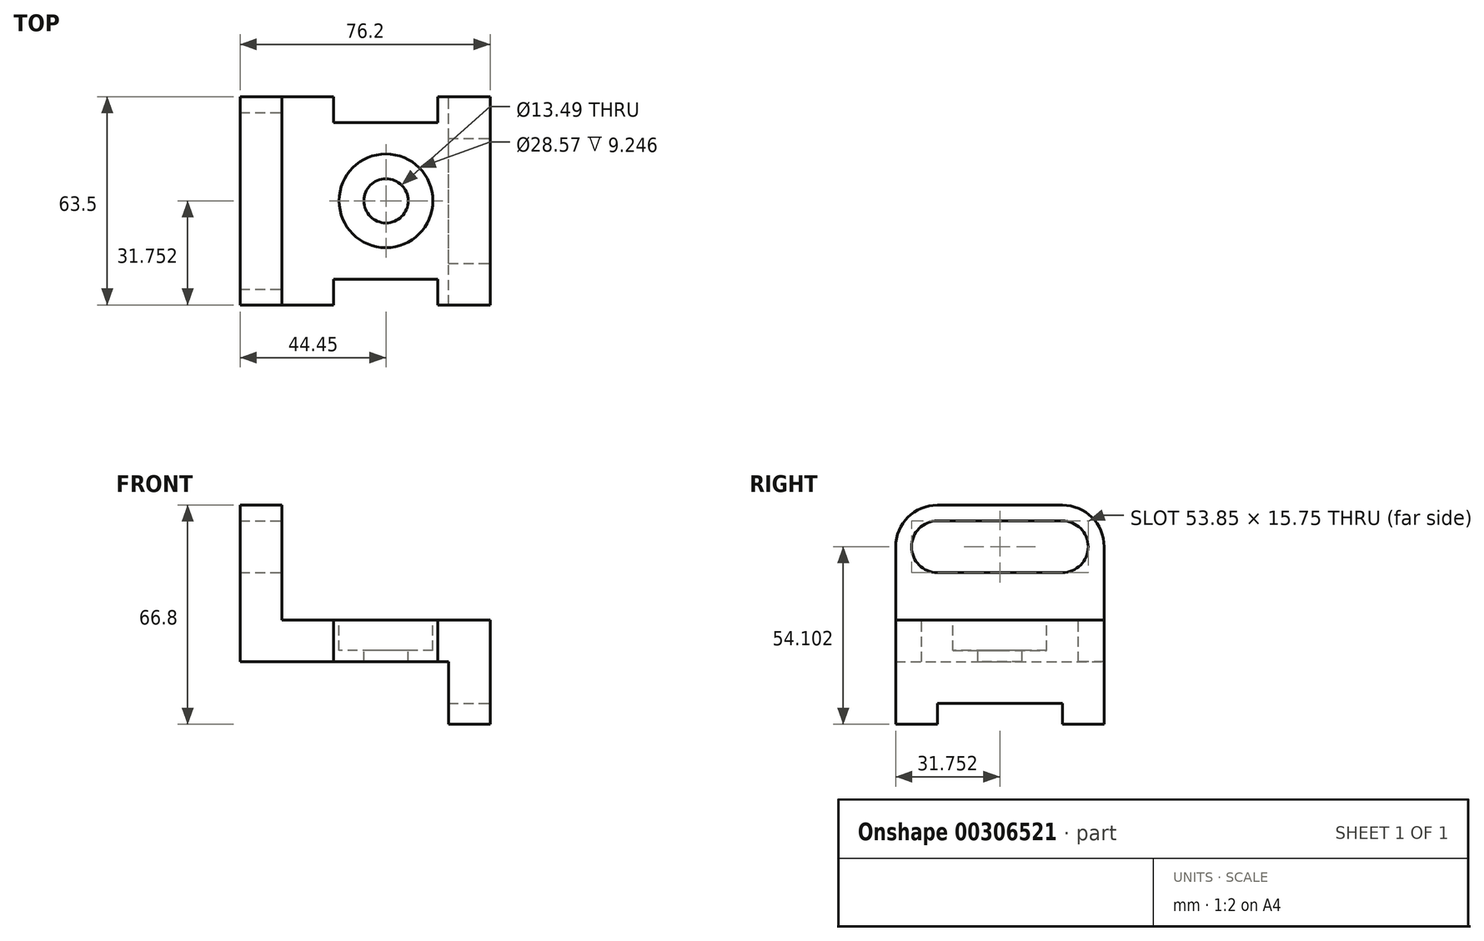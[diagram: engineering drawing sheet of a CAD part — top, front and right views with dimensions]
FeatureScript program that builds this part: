
annotation { "Feature Type Name" : "Feature", "Feature Type Description" : "" }
export const myFeature = defineFeature(function(context is Context, id is Id, definition is map)
    precondition{}
    {
        {
            var Q0;
            Q0=qCreatedBy(makeId("Top.planeOp"),FACE);
            var sketch = newSketch(context, id + "F0", { "sketchPlane" : qUnion([Q0])});
            skLineSegment(sketch, "E0.bottom", {"start": v(0, 0.53) * mm, "end": v(63.5, 0.53) * mm});
            skLineSegment(sketch, "E0.top", {"start": v(0, 64.03) * mm, "end": v(63.5, 64.03) * mm});
            skLineSegment(sketch, "E0.left", {"start": v(0, 0.53) * mm, "end": v(0, 64.03) * mm});
            skLineSegment(sketch, "E0.right", {"start": v(63.5, 0.53) * mm, "end": v(63.5, 64.03) * mm});
            skSolve(sketch);
        }
        {
            var Q0;
            Q0 = qSketchRegion(id + "F0", true);
            extrude(context, id + "F1", {"entities" : qUnion([Q0]), "depth" : 12.7 * mm});
        }
        {
            var Q0;
            Q0=qCreatedBy(makeId("Right.planeOp"),FACE);
            var sketch = newSketch(context, id + "F2", { "sketchPlane" : qUnion([Q0])});
            skArc(sketch, "E1", {"start": v(13.23, 42.93) * mm, "mid": v(5.36, 35.05) * mm, "end": v(13.23, 27.18) * mm});
            skArc(sketch, "E2", {"start": v(51.33, 27.18) * mm, "mid": v(59.2, 35.05) * mm, "end": v(51.33, 42.93) * mm});
            skArc(sketch, "E3", {"start": v(13.23, 47.75) * mm, "mid": v(4.25, 44.03) * mm, "end": v(0.53, 35.05) * mm});
            skArc(sketch, "E4", {"start": v(64.03, 35.05) * mm, "mid": v(60.31, 44.03) * mm, "end": v(51.33, 47.75) * mm});
            skLineSegment(sketch, "E5", {"start": v(13.23, 47.75) * mm, "end": v(51.33, 47.75) * mm});
            skLineSegment(sketch, "E6", {"start": v(0.53, 35.05) * mm, "end": v(0.53, 12.7) * mm});
            skLineSegment(sketch, "E7", {"start": v(0.53, 12.7) * mm, "end": v(64.03, 12.7) * mm});
            skLineSegment(sketch, "E8", {"start": v(64.03, 12.7) * mm, "end": v(64.03, 35.05) * mm});
            skLineSegment(sketch, "E9", {"start": v(13.23, 42.93) * mm, "end": v(51.33, 42.93) * mm});
            skLineSegment(sketch, "E10", {"start": v(13.23, 27.18) * mm, "end": v(51.33, 27.18) * mm});
            skSolve(sketch);
        }
        {
            var Q0;
            Q0=makeQuery(id+"F1.opExtrude","SWEPT_FACE",FACE,{"disambiguationData":[OSD([sQuery(id+"F0.wireOp",EDGE,"E0.left")])]});
            var sketch = newSketch(context, id + "F3", { "sketchPlane" : qUnion([Q0])});
            skLineSegment(sketch, "E11.bottom", {"start": v(-64.03, 0) * mm, "end": v(-0.53, 0) * mm});
            skLineSegment(sketch, "E11.top", {"start": v(-64.03, 12.7) * mm, "end": v(-0.53, 12.7) * mm});
            skLineSegment(sketch, "E11.left", {"start": v(-64.03, 0) * mm, "end": v(-64.03, 12.7) * mm});
            skLineSegment(sketch, "E11.right", {"start": v(-0.53, 0) * mm, "end": v(-0.53, 12.7) * mm});
            skSolve(sketch);
        }
        {
            var Q0;
            Q0 = qSketchRegion(id + "F3", true);
            extrude(context, id + "F4", {"entities" : qUnion([Q0]), "operationType" : NewBodyOperationType.ADD, "depth" : 12.7 * mm});
        }
        {
            var Q0;
            Q0 = qSketchRegion(id + "F2", true);
            extrude(context, id + "F5", {"entities" : qUnion([Q0]), "operationType" : NewBodyOperationType.ADD, "oppositeDirection" : true, "depth" : 12.7 * mm});
        }
        {
            var Q0;
            Q0=makeQuery(id+"F4.boolean.opBoolean","MERGE",FACE,{"derivedFrom":[makeQuery(id+"F1.opExtrude","CAP_FACE",FACE,{"disambiguationData":[OSD([sQuery(id+"F0.wireOp",EDGE,"E0.bottom"),sQuery(id+"F0.wireOp",EDGE,"E0.top"),sQuery(id+"F0.wireOp",EDGE,"E0.left"),sQuery(id+"F0.wireOp",EDGE,"E0.right")])],"isStart":false}),makeQuery(id+"F4.opExtrude","SWEPT_FACE",FACE,{"disambiguationData":[OSD([sQuery(id+"F3.wireOp",EDGE,"E11.top")])]})]});
            var sketch = newSketch(context, id + "F6", { "sketchPlane" : qUnion([Q0])});
            skLineSegment(sketch, "E12.bottom", {"start": v(15.75, 0.53) * mm, "end": v(47.5, 0.53) * mm});
            skLineSegment(sketch, "E12.top", {"start": v(15.75, 8.4) * mm, "end": v(47.5, 8.4) * mm});
            skLineSegment(sketch, "E12.left", {"start": v(15.75, 0.53) * mm, "end": v(15.75, 8.4) * mm});
            skLineSegment(sketch, "E12.right", {"start": v(47.5, 0.53) * mm, "end": v(47.5, 8.4) * mm});
            skLineSegment(sketch, "E13.bottom", {"start": v(47.5, 64.03) * mm, "end": v(15.75, 64.03) * mm});
            skLineSegment(sketch, "E13.top", {"start": v(47.5, 56.16) * mm, "end": v(15.75, 56.16) * mm});
            skLineSegment(sketch, "E13.left", {"start": v(47.5, 64.03) * mm, "end": v(47.5, 56.16) * mm});
            skLineSegment(sketch, "E13.right", {"start": v(15.75, 64.03) * mm, "end": v(15.75, 56.16) * mm});
            skSolve(sketch);
        }
        {
            var Q0;
            Q0 = qSketchRegion(id + "F6", true);
            extrude(context, id + "F7", {"entities" : qUnion([Q0]), "operationType" : NewBodyOperationType.REMOVE, "endBound" : BoundingType.THROUGH_ALL, "oppositeDirection" : true, "depth" : 25.4 * mm});
        }
        {
            var Q0;
            Q0=makeQuery(id+"F4.boolean.opBoolean","MERGE",FACE,{"derivedFrom":[makeQuery(id+"F1.opExtrude","CAP_FACE",FACE,{"disambiguationData":[OSD([sQuery(id+"F0.wireOp",EDGE,"E0.bottom"),sQuery(id+"F0.wireOp",EDGE,"E0.top"),sQuery(id+"F0.wireOp",EDGE,"E0.left"),sQuery(id+"F0.wireOp",EDGE,"E0.right")])],"isStart":true}),makeQuery(id+"F4.opExtrude","SWEPT_FACE",FACE,{"disambiguationData":[OSD([sQuery(id+"F3.wireOp",EDGE,"E11.bottom")])]})]});
            var sketch = newSketch(context, id + "F8", { "sketchPlane" : qUnion([Q0])});
            skLineSegment(sketch, "E14.bottom", {"start": v(63.5, -0.53) * mm, "end": v(50.8, -0.53) * mm});
            skLineSegment(sketch, "E14.top", {"start": v(63.5, -64.03) * mm, "end": v(50.8, -64.03) * mm});
            skLineSegment(sketch, "E14.left", {"start": v(63.5, -0.53) * mm, "end": v(63.5, -64.03) * mm});
            skLineSegment(sketch, "E14.right", {"start": v(50.8, -0.53) * mm, "end": v(50.8, -64.03) * mm});
            skSolve(sketch);
        }
        {
            var Q0;
            Q0 = qSketchRegion(id + "F8", true);
            extrude(context, id + "F9", {"entities" : qUnion([Q0]), "operationType" : NewBodyOperationType.ADD, "depth" : 19.05 * mm});
        }
        {
            var Q0;
            Q0=makeQuery(id+"F9.boolean.opBoolean","MERGE",FACE,{"derivedFrom":[makeQuery(id+"F1.opExtrude","SWEPT_FACE",FACE,{"disambiguationData":[OSD([sQuery(id+"F0.wireOp",EDGE,"E0.right")])]}),makeQuery(id+"F9.opExtrude","SWEPT_FACE",FACE,{"disambiguationData":[OSD([sQuery(id+"F8.wireOp",EDGE,"E14.left")])]})]});
            var sketch = newSketch(context, id + "F10", { "sketchPlane" : qUnion([Q0])});
            skLineSegment(sketch, "E15.bottom", {"start": v(13.23, -19.05) * mm, "end": v(51.33, -19.05) * mm});
            skLineSegment(sketch, "E15.top", {"start": v(13.23, -12.7) * mm, "end": v(51.33, -12.7) * mm});
            skLineSegment(sketch, "E15.left", {"start": v(13.23, -19.05) * mm, "end": v(13.23, -12.7) * mm});
            skLineSegment(sketch, "E15.right", {"start": v(51.33, -19.05) * mm, "end": v(51.33, -12.7) * mm});
            skSolve(sketch);
        }
        {
            var Q0;
            Q0 = qSketchRegion(id + "F10", true);
            extrude(context, id + "F11", {"entities" : qUnion([Q0]), "operationType" : NewBodyOperationType.REMOVE, "oppositeDirection" : true, "depth" : 25.4 * mm});
        }
        {
            var Q0;
            Q0=makeQuery(id+"F4.boolean.opBoolean","MERGE",FACE,{"derivedFrom":[makeQuery(id+"F1.opExtrude","CAP_FACE",FACE,{"disambiguationData":[OSD([sQuery(id+"F0.wireOp",EDGE,"E0.bottom"),sQuery(id+"F0.wireOp",EDGE,"E0.top"),sQuery(id+"F0.wireOp",EDGE,"E0.left"),sQuery(id+"F0.wireOp",EDGE,"E0.right")])],"isStart":false}),makeQuery(id+"F4.opExtrude","SWEPT_FACE",FACE,{"disambiguationData":[OSD([sQuery(id+"F3.wireOp",EDGE,"E11.top")])]})]});
            var sketch = newSketch(context, id + "F12", { "sketchPlane" : qUnion([Q0])});
            skCircle(sketch, "E16", {"center": v(31.75, 32.28) * mm, "radius": 6.74 * mm});
            skSolve(sketch);
        }
        {
            var Q0;
            Q0 = qSketchRegion(id + "F12", true);
            extrude(context, id + "F13", {"entities" : qUnion([Q0]), "operationType" : NewBodyOperationType.REMOVE, "endBound" : BoundingType.THROUGH_ALL, "oppositeDirection" : true, "depth" : 25.4 * mm});
        }
        {
            var Q0;
            Q0=makeQuery(id+"F4.boolean.opBoolean","MERGE",FACE,{"derivedFrom":[makeQuery(id+"F1.opExtrude","CAP_FACE",FACE,{"disambiguationData":[OSD([sQuery(id+"F0.wireOp",EDGE,"E0.bottom"),sQuery(id+"F0.wireOp",EDGE,"E0.top"),sQuery(id+"F0.wireOp",EDGE,"E0.left"),sQuery(id+"F0.wireOp",EDGE,"E0.right")])],"isStart":false}),makeQuery(id+"F4.opExtrude","SWEPT_FACE",FACE,{"disambiguationData":[OSD([sQuery(id+"F3.wireOp",EDGE,"E11.top")])]})]});
            var sketch = newSketch(context, id + "F14", { "sketchPlane" : qUnion([Q0])});
            skCircle(sketch, "E17", {"center": v(31.75, 32.28) * mm, "radius": 14.29 * mm});
            skSolve(sketch);
        }
        {
            var Q0;
            Q0 = qSketchRegion(id + "F14", true);
            extrude(context, id + "F15", {"entities" : qUnion([Q0]), "operationType" : NewBodyOperationType.REMOVE, "oppositeDirection" : true, "depth" : 9.25 * mm});
        }
    });
